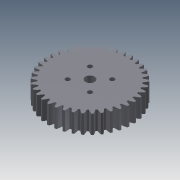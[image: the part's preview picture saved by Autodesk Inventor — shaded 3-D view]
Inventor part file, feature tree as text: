
AUTODESK INVENTOR PART (.ipt)
format: ipt  version: 2015 (Build 190159000, 159)  size: 516,096 bytes
history: native  units: mm (DEFAULTED — no unit token found)
features: other x8, sketch x4, plane x3, extrude x2, projected_geometry x1
ambient origin geometry x8: Origin, YZ Plane, XZ Plane, XY Plane, X Axis, Y Axis, Z Axis, Center Point
bodies: Solid1 (feature_tree)
feature tree (18):
  other  "Blocks"
  extrude  "Extrusion1"  Depth=20.0mm TaperAngle=0.0deg
  plane  "Work Plane2"
  plane  "Work Plane8"
  plane  "Work Plane9"
  other  "Spur Gear"
  extrude  "Extrusion3"  Depth=10.0mm TaperAngle=0.0deg
  sketch  "Sketch4"  dims[d17=0.0mm d34=0.826735mm d39=0.0mm d41=0.0mm d43=70.0mm d46=70.0mm d47=0.0mm d48=0.0mm d51=10.0mm d52=5.0mm d53=15.0mm d54=15.0mm d55=5.0mm d56=12.0mm d57=12.0mm d58=10.0mm d59=0.0mm]
  other  "DXF"
  sketch  "Sketch1"  dims[d0=90.5mm d1=20.0mm d2=0.0mm]
  sketch  "Sketch2"  dims[d3=85.806452mm d4=10.0mm d5=0.0mm]
  other  "Srf1"
  sketch  "Sketch3"  dims[d16=70.0mm]
  projected_geometry  "Projected Loop1"
  other  "Block1"
  other  "Pitch Diameter"
  other  "Block1:1"
  other  "Block1:2"
